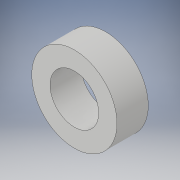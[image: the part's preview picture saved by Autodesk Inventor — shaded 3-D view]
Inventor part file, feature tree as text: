
AUTODESK INVENTOR PART (.ipt)
format: ipt  version: 2019 (Build 230136000, 136)  size: 101,888 bytes
history: native  units: mm
features: extrude x2, sketch x2
ambient origin geometry x8: Origin, YZ Plane, XZ Plane, XY Plane, X Axis, Y Axis, Z Axis, Center Point
bodies: Solid1 (feature_tree)
feature tree (4):
  extrude  "Extrusion1"  Depth=14.4mm TaperAngle=0.0deg
  extrude  "Extrusion2"  Depth=14.4mm TaperAngle=0.0deg
  sketch  "Sketch1"  dims[d0=39.2mm d1=14.4mm d2=0.0mm]
  sketch  "Sketch3"  dims[d3=22.4mm d4=14.4mm d5=0.0mm]
